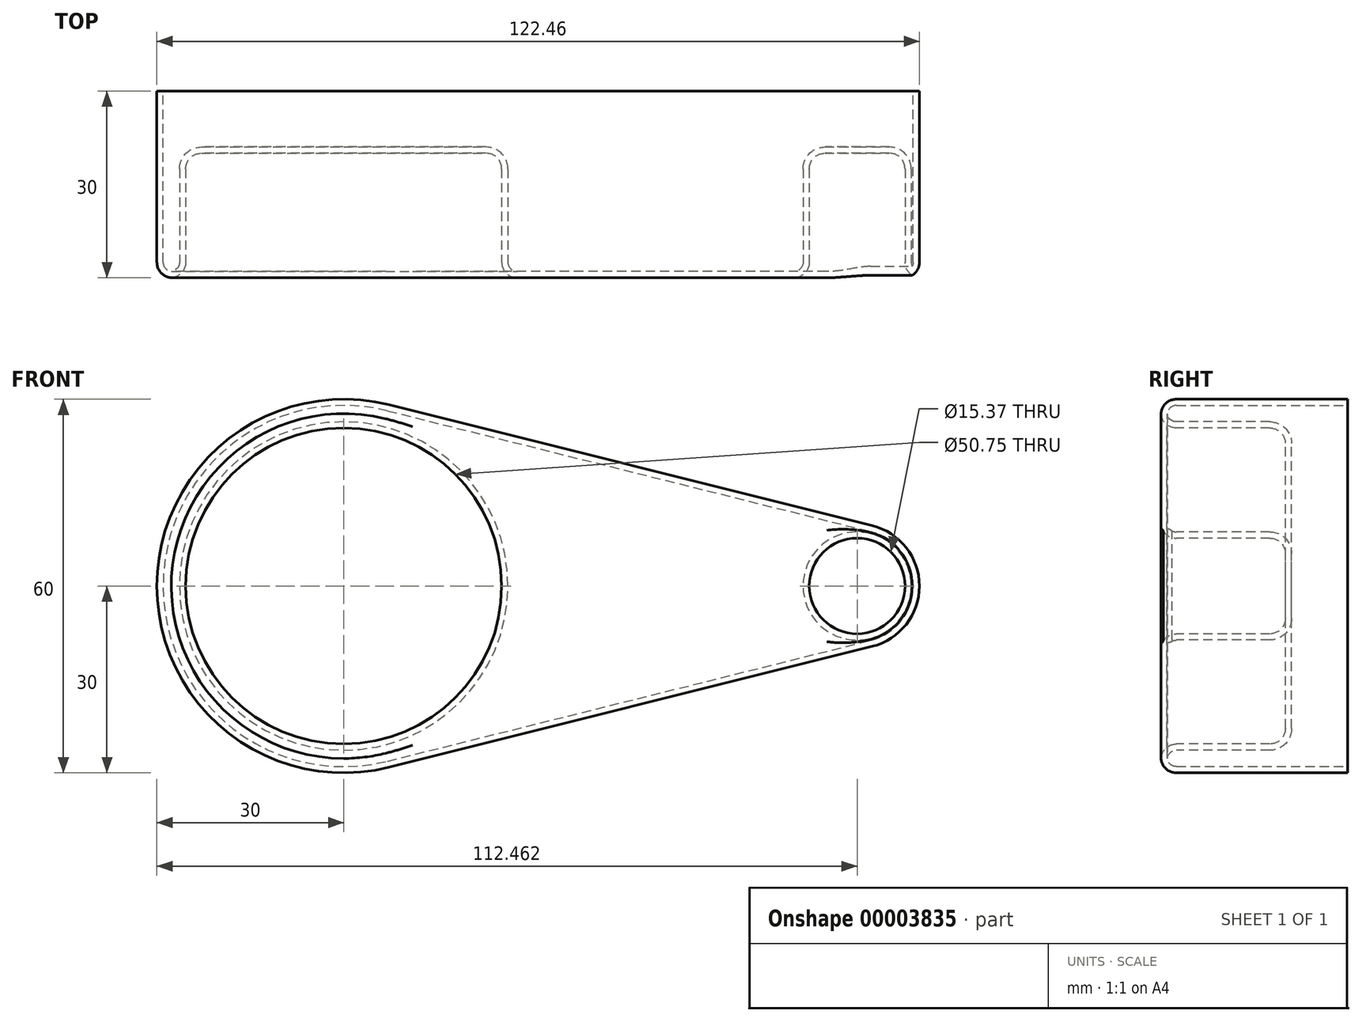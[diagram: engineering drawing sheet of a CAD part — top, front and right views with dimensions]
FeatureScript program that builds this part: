
annotation { "Feature Type Name" : "Feature", "Feature Type Description" : "" }
export const myFeature = defineFeature(function(context is Context, id is Id, definition is map)
    precondition{}
    {
        {
            var Q0;
            Q0=qCreatedBy(makeId("Front.planeOp"),FACE);
            var sketch = newSketch(context, id + "F0", { "sketchPlane" : qUnion([Q0])});
            skCircle(sketch, "E0", {"center": v(0, 0) * mm, "radius": 30 * mm});
            skCircle(sketch, "E1", {"center": v(82.46, 0) * mm, "radius": 10 * mm});
            skLineSegment(sketch, "E2", {"start": v(7.28, 29.1) * mm, "end": v(84.89, 9.7) * mm});
            skLineSegment(sketch, "E3", {"start": v(7.28, -29.1) * mm, "end": v(84.89, -9.7) * mm});
            skSolve(sketch);
        }
        {
            var Q0;
            {var subQ0=sQuery(id+"F0.wireOp",EDGE,"E0");var subQ2=makeQuery(id+"F0.imprint","INTERSECT",VERTEX,{"derivedFrom":[subQ0,sQuery(id+"F0.wireOp",EDGE,"E2")]});Q0=makeQuery(id+"F0.imprint","IMPRINT",FACE,{"disambiguationData":[TD([[makeQuery(id+"F0.imprint","IMPRINT",EDGE,{"disambiguationData":[TD([[subQ2,-1.0]])],"derivedFrom":subQ0}),1.0]])]});}
            var Q1;
            {var subQ1=sQuery(id+"F0.wireOp",EDGE,"E2");Q1=makeQuery(id+"F0.imprint","IMPRINT",FACE,{"disambiguationData":[TD([[makeQuery(id+"F0.imprint","IMPRINT",EDGE,{"derivedFrom":subQ1}),-1.0]])]});}
            var Q2;
            {var subQ0=sQuery(id+"F0.wireOp",EDGE,"E1");var subQ2=makeQuery(id+"F0.imprint","INTERSECT",VERTEX,{"derivedFrom":[subQ0,sQuery(id+"F0.wireOp",EDGE,"E2")]});Q2=makeQuery(id+"F0.imprint","IMPRINT",FACE,{"disambiguationData":[TD([[makeQuery(id+"F0.imprint","IMPRINT",EDGE,{"disambiguationData":[TD([[subQ2,-1.0]])],"derivedFrom":subQ0}),1.0]])]});}
            extrude(context, id + "F1", {"entities" : qUnion([Q0, Q1, Q2]), "depth" : 30 * mm});
        }
        {
            var Q0;
            Q0=makeQuery(id+"F1.opExtrude","CAP_FACE",FACE,{"disambiguationData":[OSD([sQuery(id+"F0.wireOp",EDGE,"E0"),sQuery(id+"F0.wireOp",EDGE,"E1"),sQuery(id+"F0.wireOp",EDGE,"E2"),sQuery(id+"F0.wireOp",EDGE,"E3")])],"isStart":false});
            var sketch = newSketch(context, id + "F2", { "sketchPlane" : qUnion([Q0])});
            skCircle(sketch, "E4", {"center": v(0, 0) * mm, "radius": 25.37 * mm});
            skCircle(sketch, "E5", {"center": v(82.46, 0) * mm, "radius": 7.69 * mm});
            skSolve(sketch);
        }
        {
            var Q0;
            Q0=makeQuery(id+"F2.imprint","IMPRINT",FACE,{"disambiguationData":[TD([[makeQuery(id+"F2.imprint","IMPRINT",EDGE,{"derivedFrom":sQuery(id+"F2.wireOp",EDGE,"E4")}),1.0]])]});
            var Q1;
            Q1=makeQuery(id+"F2.imprint","IMPRINT",FACE,{"disambiguationData":[TD([[makeQuery(id+"F2.imprint","IMPRINT",EDGE,{"derivedFrom":sQuery(id+"F2.wireOp",EDGE,"E5")}),1.0]])]});
            extrude(context, id + "F3", {"entities" : qUnion([Q0, Q1]), "operationType" : NewBodyOperationType.REMOVE, "oppositeDirection" : true, "depth" : 20 * mm});
        }
        {
            var Q0;
            Q0=makeQuery(id+"F1.opExtrude","CAP_FACE",FACE,{"disambiguationData":[OSD([sQuery(id+"F0.wireOp",EDGE,"E0"),sQuery(id+"F0.wireOp",EDGE,"E1"),sQuery(id+"F0.wireOp",EDGE,"E2"),sQuery(id+"F0.wireOp",EDGE,"E3")])],"isStart":false});
            var Q1;
            Q1=makeQuery(id+"F3.boolean.opBoolean","COPY",EDGE,{"derivedFrom":makeQuery(id+"F3.opExtrude","CAP_EDGE",EDGE,{"disambiguationData":[OSD([sQuery(id+"F2.wireOp",EDGE,"E4")])],"isStart":false})});
            var Q2;
            Q2=makeQuery(id+"F3.boolean.opBoolean","COPY",EDGE,{"derivedFrom":makeQuery(id+"F3.opExtrude","CAP_EDGE",EDGE,{"disambiguationData":[OSD([sQuery(id+"F2.wireOp",EDGE,"E5")])],"isStart":false})});
            fillet(context, id + "F4", {"entities" : qUnion([Q0, Q1, Q2]), "radius" : 2.5 * mm, "tangentPropagation" : true, "allowEdgeOverflow" : false});
        }
        {
            var Q0;
            Q0=makeQuery(id+"F1.opExtrude","CAP_FACE",FACE,{"disambiguationData":[OSD([sQuery(id+"F0.wireOp",EDGE,"E0"),sQuery(id+"F0.wireOp",EDGE,"E1"),sQuery(id+"F0.wireOp",EDGE,"E2"),sQuery(id+"F0.wireOp",EDGE,"E3")])],"isStart":true});
            shell(context, id + "F5", {"entities" : qUnion([Q0]), "thickness" : 1 * mm});
        }
    });
